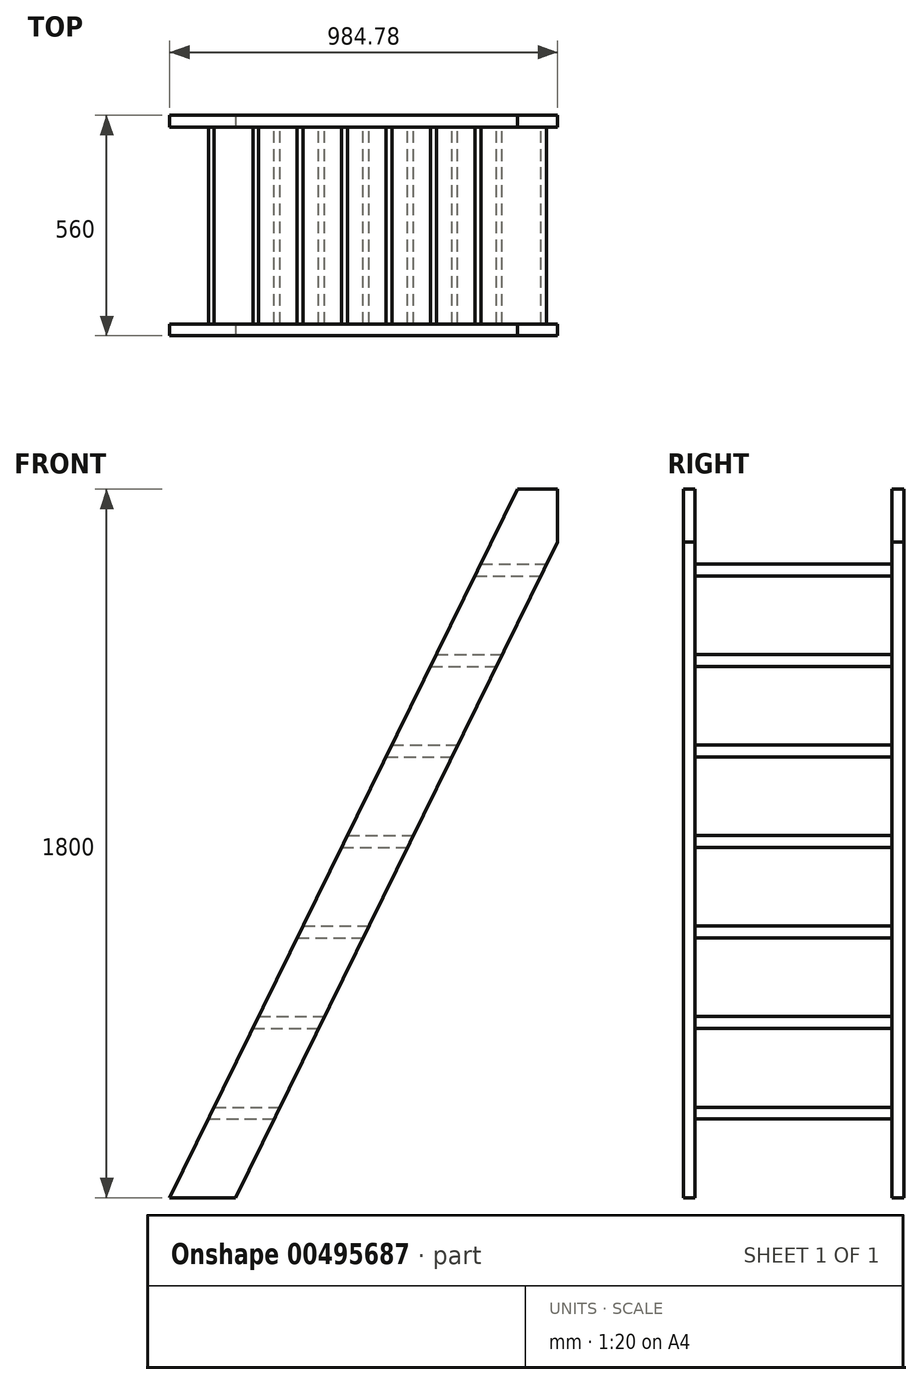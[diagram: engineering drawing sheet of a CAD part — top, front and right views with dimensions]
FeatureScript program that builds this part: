
annotation { "Feature Type Name" : "Feature", "Feature Type Description" : "" }
export const myFeature = defineFeature(function(context is Context, id is Id, definition is map)
    precondition{}
    {
        {
            var Q0;
            Q0=qCreatedBy(makeId("Front.planeOp"),FACE);
            var sketch = newSketch(context, id + "F0", { "sketchPlane" : qUnion([Q0])});
            skLineSegment(sketch, "E0.right", {"start": v(500, 900) * mm, "end": v(500, 766.36) * mm});
            skPoint(sketch, "E0.middle", {"position": v(0, 0) * mm});
            skLineSegment(sketch, "E1", {"start": v(500, 766.36) * mm, "end": v(-317.7, -900) * mm});
            skLineSegment(sketch, "E2.0", {"start": v(365.34, 832.44) * mm, "end": v(-452.36, -833.92) * mm});
            skLineSegment(sketch, "E3", {"start": v(365.34, 832.44) * mm, "end": v(398.5, 900) * mm});
            skLineSegment(sketch, "E4", {"start": v(-452.36, -833.92) * mm, "end": v(-484.78, -900) * mm});
            skLineSegment(sketch, "E5", {"start": v(398.5, 900) * mm, "end": v(500, 900) * mm});
            skLineSegment(sketch, "E6", {"start": v(-386.64, -700) * mm, "end": v(-219.55, -700) * mm});
            skLineSegment(sketch, "E7", {"start": v(-371.92, -670) * mm, "end": v(-204.83, -670) * mm});
            skLineSegment(sketch, "E8.0", {"start": v(-273.78, -470) * mm, "end": v(-106.7, -470) * mm});
            skLineSegment(sketch, "E9.0", {"start": v(-259.06, -440) * mm, "end": v(-91.97, -440) * mm});
            skLineSegment(sketch, "E10.0", {"start": v(-146.2, -210) * mm, "end": v(20.9, -210) * mm});
            skLineSegment(sketch, "E11.0", {"start": v(-160.92, -240) * mm, "end": v(6.17, -240) * mm});
            skLineSegment(sketch, "E12.0", {"start": v(-33.33, 20) * mm, "end": v(133.75, 20) * mm});
            skLineSegment(sketch, "E13.0", {"start": v(-48.05, -10) * mm, "end": v(119.03, -10) * mm});
            skLineSegment(sketch, "E14.0", {"start": v(79.53, 250) * mm, "end": v(246.62, 250) * mm});
            skLineSegment(sketch, "E15.0", {"start": v(64.8, 220) * mm, "end": v(231.9, 220) * mm});
            skLineSegment(sketch, "E16.0", {"start": v(192.4, 480) * mm, "end": v(359.48, 480) * mm});
            skLineSegment(sketch, "E17.0", {"start": v(177.67, 450) * mm, "end": v(344.76, 450) * mm});
            skLineSegment(sketch, "E18.0", {"start": v(305.26, 710) * mm, "end": v(472.34, 710) * mm});
            skLineSegment(sketch, "E19.0", {"start": v(290.53, 680) * mm, "end": v(457.62, 680) * mm});
            skPoint(sketch, "E20.orphan", {"position": v(500, -900) * mm});
            skLineSegment(sketch, "E21", {"start": v(-317.7, -900) * mm, "end": v(-484.78, -900) * mm});
            skSolve(sketch);
        }
        {
            var Q0;
            {var subQ0=sQuery(id+"F0.wireOp",EDGE,"E6");Q0=makeQuery(id+"F0.imprint","IMPRINT",FACE,{"disambiguationData":[TD([[makeQuery(id+"F0.imprint","IMPRINT",EDGE,{"derivedFrom":subQ0}),1.0]])]});}
            var Q1;
            {var subQ0=sQuery(id+"F0.wireOp",EDGE,"E8.0");Q1=makeQuery(id+"F0.imprint","IMPRINT",FACE,{"disambiguationData":[TD([[makeQuery(id+"F0.imprint","IMPRINT",EDGE,{"derivedFrom":subQ0}),1.0]])]});}
            var Q2;
            {var subQ0=sQuery(id+"F0.wireOp",EDGE,"E10.0");Q2=makeQuery(id+"F0.imprint","IMPRINT",FACE,{"disambiguationData":[TD([[makeQuery(id+"F0.imprint","IMPRINT",EDGE,{"derivedFrom":subQ0}),-1.0]])]});}
            var Q3;
            {var subQ0=sQuery(id+"F0.wireOp",EDGE,"E12.0");Q3=makeQuery(id+"F0.imprint","IMPRINT",FACE,{"disambiguationData":[TD([[makeQuery(id+"F0.imprint","IMPRINT",EDGE,{"derivedFrom":subQ0}),-1.0]])]});}
            var Q4;
            {var subQ0=sQuery(id+"F0.wireOp",EDGE,"E14.0");Q4=makeQuery(id+"F0.imprint","IMPRINT",FACE,{"disambiguationData":[TD([[makeQuery(id+"F0.imprint","IMPRINT",EDGE,{"derivedFrom":subQ0}),-1.0]])]});}
            var Q5;
            {var subQ0=sQuery(id+"F0.wireOp",EDGE,"E16.0");Q5=makeQuery(id+"F0.imprint","IMPRINT",FACE,{"disambiguationData":[TD([[makeQuery(id+"F0.imprint","IMPRINT",EDGE,{"derivedFrom":subQ0}),-1.0]])]});}
            var Q6;
            {var subQ0=sQuery(id+"F0.wireOp",EDGE,"E18.0");Q6=makeQuery(id+"F0.imprint","IMPRINT",FACE,{"disambiguationData":[TD([[makeQuery(id+"F0.imprint","IMPRINT",EDGE,{"derivedFrom":subQ0}),-1.0]])]});}
            extrude(context, id + "F1", {"entities" : qUnion([Q0, Q1, Q2, Q3, Q4, Q5, Q6]), "depth" : 500 * mm});
        }
        {
            var Q0;
            {var subQ4=sQuery(id+"F0.wireOp",EDGE,"E0.right");Q0=makeQuery(id+"F0.imprint","IMPRINT",FACE,{"disambiguationData":[TD([[makeQuery(id+"F0.imprint","IMPRINT",EDGE,{"derivedFrom":subQ4}),-1.0]])]});}
            var Q1;
            {var subQ0=sQuery(id+"F0.wireOp",EDGE,"E18.0");Q1=makeQuery(id+"F0.imprint","IMPRINT",FACE,{"disambiguationData":[TD([[makeQuery(id+"F0.imprint","IMPRINT",EDGE,{"derivedFrom":subQ0}),-1.0]])]});}
            var Q2;
            {var subQ0=sQuery(id+"F0.wireOp",EDGE,"E16.0");Q2=makeQuery(id+"F0.imprint","IMPRINT",FACE,{"disambiguationData":[TD([[makeQuery(id+"F0.imprint","IMPRINT",EDGE,{"derivedFrom":subQ0}),1.0]])]});}
            var Q3;
            {var subQ0=sQuery(id+"F0.wireOp",EDGE,"E16.0");Q3=makeQuery(id+"F0.imprint","IMPRINT",FACE,{"disambiguationData":[TD([[makeQuery(id+"F0.imprint","IMPRINT",EDGE,{"derivedFrom":subQ0}),-1.0]])]});}
            var Q4;
            {var subQ0=sQuery(id+"F0.wireOp",EDGE,"E14.0");Q4=makeQuery(id+"F0.imprint","IMPRINT",FACE,{"disambiguationData":[TD([[makeQuery(id+"F0.imprint","IMPRINT",EDGE,{"derivedFrom":subQ0}),1.0]])]});}
            var Q5;
            {var subQ0=sQuery(id+"F0.wireOp",EDGE,"E14.0");Q5=makeQuery(id+"F0.imprint","IMPRINT",FACE,{"disambiguationData":[TD([[makeQuery(id+"F0.imprint","IMPRINT",EDGE,{"derivedFrom":subQ0}),-1.0]])]});}
            var Q6;
            {var subQ0=sQuery(id+"F0.wireOp",EDGE,"E12.0");Q6=makeQuery(id+"F0.imprint","IMPRINT",FACE,{"disambiguationData":[TD([[makeQuery(id+"F0.imprint","IMPRINT",EDGE,{"derivedFrom":subQ0}),1.0]])]});}
            var Q7;
            {var subQ0=sQuery(id+"F0.wireOp",EDGE,"E12.0");Q7=makeQuery(id+"F0.imprint","IMPRINT",FACE,{"disambiguationData":[TD([[makeQuery(id+"F0.imprint","IMPRINT",EDGE,{"derivedFrom":subQ0}),-1.0]])]});}
            var Q8;
            {var subQ0=sQuery(id+"F0.wireOp",EDGE,"E10.0");Q8=makeQuery(id+"F0.imprint","IMPRINT",FACE,{"disambiguationData":[TD([[makeQuery(id+"F0.imprint","IMPRINT",EDGE,{"derivedFrom":subQ0}),1.0]])]});}
            var Q9;
            {var subQ0=sQuery(id+"F0.wireOp",EDGE,"E10.0");Q9=makeQuery(id+"F0.imprint","IMPRINT",FACE,{"disambiguationData":[TD([[makeQuery(id+"F0.imprint","IMPRINT",EDGE,{"derivedFrom":subQ0}),-1.0]])]});}
            var Q10;
            {var subQ0=sQuery(id+"F0.wireOp",EDGE,"E9.0");Q10=makeQuery(id+"F0.imprint","IMPRINT",FACE,{"disambiguationData":[TD([[makeQuery(id+"F0.imprint","IMPRINT",EDGE,{"derivedFrom":subQ0}),1.0]])]});}
            var Q11;
            {var subQ0=sQuery(id+"F0.wireOp",EDGE,"E8.0");Q11=makeQuery(id+"F0.imprint","IMPRINT",FACE,{"disambiguationData":[TD([[makeQuery(id+"F0.imprint","IMPRINT",EDGE,{"derivedFrom":subQ0}),1.0]])]});}
            var Q12;
            {var subQ0=sQuery(id+"F0.wireOp",EDGE,"E7");Q12=makeQuery(id+"F0.imprint","IMPRINT",FACE,{"disambiguationData":[TD([[makeQuery(id+"F0.imprint","IMPRINT",EDGE,{"derivedFrom":subQ0}),1.0]])]});}
            var Q13;
            {var subQ0=sQuery(id+"F0.wireOp",EDGE,"E6");Q13=makeQuery(id+"F0.imprint","IMPRINT",FACE,{"disambiguationData":[TD([[makeQuery(id+"F0.imprint","IMPRINT",EDGE,{"derivedFrom":subQ0}),1.0]])]});}
            var Q14;
            {var subQ1=sQuery(id+"F0.wireOp",EDGE,"E4");Q14=makeQuery(id+"F0.imprint","IMPRINT",FACE,{"disambiguationData":[TD([[makeQuery(id+"F0.imprint","IMPRINT",EDGE,{"derivedFrom":subQ1}),1.0]])]});}
            extrude(context, id + "F2", {"entities" : qUnion([Q0, Q1, Q2, Q3, Q4, Q5, Q6, Q7, Q8, Q9, Q10, Q11, Q12, Q13, Q14]), "depth" : -30 * mm});
        }
        {
            var Q0;
            Q0=makeQuery(id+"F2.opExtrude","SWEPT_BODY",BODY,{"disambiguationData":[OSD([sQuery(id+"F0.wireOp",EDGE,"E0.right"),sQuery(id+"F0.wireOp",EDGE,"E1"),sQuery(id+"F0.wireOp",EDGE,"E2.0"),sQuery(id+"F0.wireOp",EDGE,"E3"),sQuery(id+"F0.wireOp",EDGE,"E4"),sQuery(id+"F0.wireOp",EDGE,"E5"),sQuery(id+"F0.wireOp",EDGE,"E21")])]});
            transform(context, id + "F3", {"entities" : qUnion([Q0]), "transformType" : TransformType.TRANSLATION_3D, "dx" : 0 * mm, "dy" : -530 * mm, "dz" : 0 * mm, "makeCopy" : true});
        }
    });
